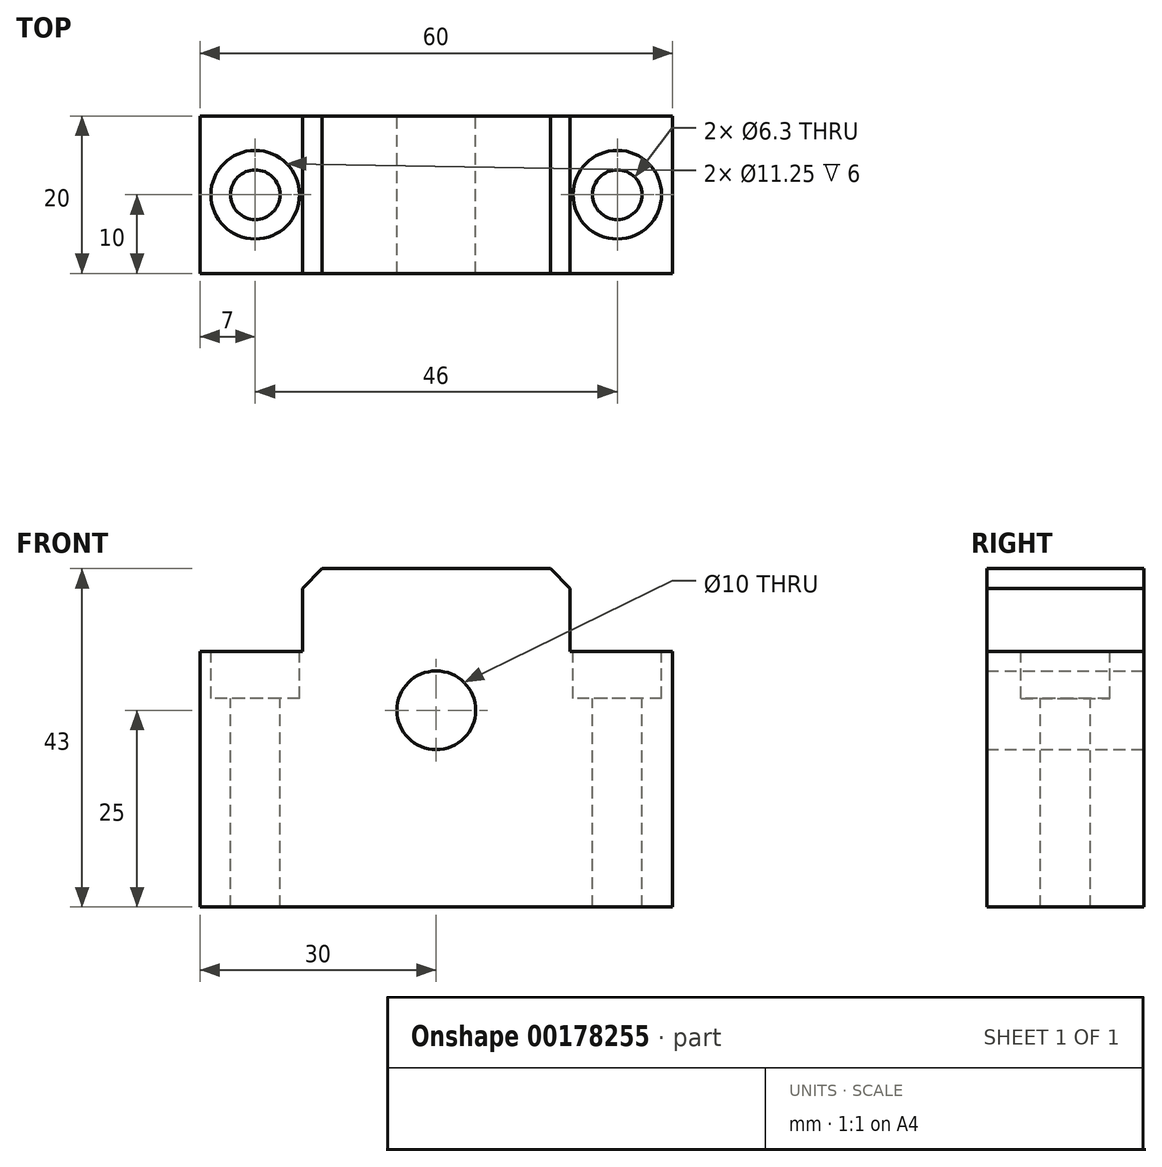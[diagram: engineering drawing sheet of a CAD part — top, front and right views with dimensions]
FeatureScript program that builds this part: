
annotation { "Feature Type Name" : "Feature", "Feature Type Description" : "" }
export const myFeature = defineFeature(function(context is Context, id is Id, definition is map)
    precondition{}
    {
        {
            var Q0;
            Q0=qCreatedBy(makeId("Front.planeOp"),FACE);
            var sketch = newSketch(context, id + "F0", { "sketchPlane" : qUnion([Q0])});
            skLineSegment(sketch, "E0.bottom", {"start": v(-30, -16.25) * mm, "end": v(30, -16.25) * mm});
            skLineSegment(sketch, "E0.top", {"start": v(-30, 16.25) * mm, "end": v(-17, 16.25) * mm});
            skLineSegment(sketch, "E0.left", {"start": v(-30, -16.25) * mm, "end": v(-30, 16.25) * mm});
            skLineSegment(sketch, "E0.right", {"start": v(30, -16.25) * mm, "end": v(30, 16.25) * mm});
            skPoint(sketch, "E0.middle", {"position": v(0, 0) * mm});
            skLineSegment(sketch, "E1.bottom", {"start": v(-17, 26.75) * mm, "end": v(17, 26.75) * mm});
            skLineSegment(sketch, "E1.left", {"start": v(-17, 26.75) * mm, "end": v(-17, 16.25) * mm});
            skLineSegment(sketch, "E1.right", {"start": v(17, 26.75) * mm, "end": v(17, 16.25) * mm});
            skLineSegment(sketch, "E2.trimOffspring", {"start": v(17, 16.25) * mm, "end": v(30, 16.25) * mm});
            skLineSegment(sketch, "E3", {"start": v(0, 26.75) * mm, "end": v(0, -16.25) * mm, "construction": true});
            skLineSegment(sketch, "E4", {"start": v(-30, 8.75) * mm, "end": v(30, 8.75) * mm, "construction": true});
            skCircle(sketch, "E5", {"center": v(0, 8.75) * mm, "radius": 5 * mm});
            skSolve(sketch);
        }
        {
            var Q0;
            Q0=makeQuery(id+"F0.imprint","IMPRINT",FACE,{"disambiguationData":[TD([[makeQuery(id+"F0.imprint","IMPRINT",EDGE,{"derivedFrom":sQuery(id+"F0.wireOp",EDGE,"E0.bottom")}),1.0]])]});
            extrude(context, id + "F1", {"entities" : qUnion([Q0]), "depth" : 20 * mm});
        }
        {
            var Q0;
            Q0=makeQuery(id+"F1.opExtrude","SWEPT_FACE",FACE,{"disambiguationData":[OSD([sQuery(id+"F0.wireOp",EDGE,"E2.trimOffspring")])]});
            var sketch = newSketch(context, id + "F2", { "sketchPlane" : qUnion([Q0])});
            skLineSegment(sketch, "E6", {"start": v(30, -10) * mm, "end": v(-30, -10) * mm, "construction": true});
            skLineSegment(sketch, "E7", {"start": v(23, -20) * mm, "end": v(23, 0) * mm, "construction": true});
            skLineSegment(sketch, "E8", {"start": v(-23, -20) * mm, "end": v(-23, 0) * mm, "construction": true});
            skLineSegment(sketch, "E9", {"start": v(0, 0) * mm, "end": v(0, -20) * mm, "construction": true});
            skPoint(sketch, "E10", {"position": v(-23, -10) * mm});
            skPoint(sketch, "E10.positionSnap0", {"position": v(-23, -10) * mm});
            skPoint(sketch, "E11", {"position": v(23, -10) * mm});
            skSolve(sketch);
        }
        {
            var Q0;
            Q0=sQuery(id+"F2.wireOp",VERTEX,"E11");
            var Q1;
            Q1=sQuery(id+"F2.wireOp",VERTEX,"E10.positionSnap0");
            var Q2;
            Q2=makeQuery(id+"F1.opExtrude","SWEPT_BODY",BODY,{"disambiguationData":[OSD([sQuery(id+"F0.wireOp",EDGE,"E0.bottom"),sQuery(id+"F0.wireOp",EDGE,"E0.top"),sQuery(id+"F0.wireOp",EDGE,"E0.left"),sQuery(id+"F0.wireOp",EDGE,"E0.right"),sQuery(id+"F0.wireOp",EDGE,"E1.bottom"),sQuery(id+"F0.wireOp",EDGE,"E1.left"),sQuery(id+"F0.wireOp",EDGE,"E1.right"),sQuery(id+"F0.wireOp",EDGE,"E2.trimOffspring"),sQuery(id+"F0.wireOp",EDGE,"E5")])]});
            hole(context, id + "F3", {"style" : HoleStyle.C_BORE, "endStyle" : HoleEndStyle.THROUGH, "standardTappedOrClearance" : lookupTablePath({ "standard" : "ISO", "fit" : "Close", "size" : "M6", "type" : "Clearance" }), "standardBlindInLast" : lookupTablePath({ "fit" : "Close", "standard" : "ISO", "size" : "M6", "type" : "Clearance" }), "holeDiameter" : 6.3 * mm, "cBoreDiameter" : 11.25 * mm, "cBoreDepth" : 6 * mm, "locations" : qUnion([Q0, Q1]), "scope" : qUnion([Q2]), "isTappedThrough" : true});
        }
        {
            var Q0;
            Q0=makeQuery(id+"F1.opExtrude","SWEPT_EDGE",EDGE,{"disambiguationData":[OSD([sQuery(id+"F0.wireOp",EDGE,"E1.bottom"),sQuery(id+"F0.wireOp",EDGE,"E1.right")])]});
            var Q1;
            Q1=makeQuery(id+"F1.opExtrude","SWEPT_EDGE",EDGE,{"disambiguationData":[OSD([sQuery(id+"F0.wireOp",EDGE,"E1.bottom"),sQuery(id+"F0.wireOp",EDGE,"E1.left")])]});
            chamfer(context, id + "F4", {"entities" : qUnion([Q0, Q1]), "width" : 2.5 * mm, "tangentPropagation" : true});
        }
    });
